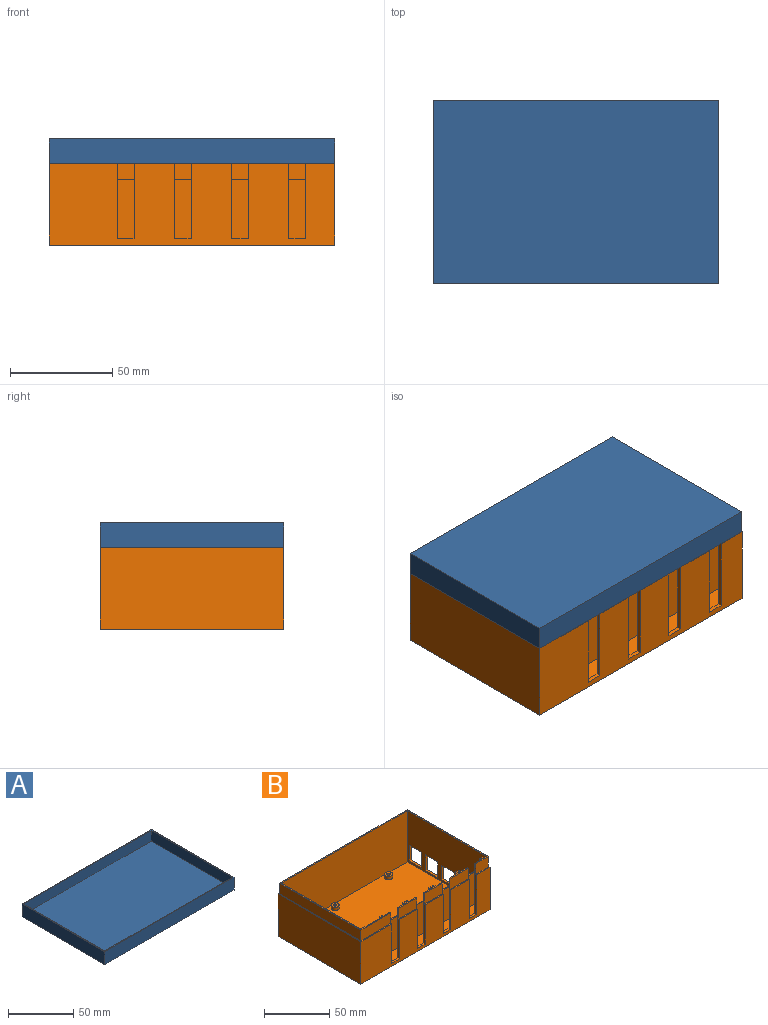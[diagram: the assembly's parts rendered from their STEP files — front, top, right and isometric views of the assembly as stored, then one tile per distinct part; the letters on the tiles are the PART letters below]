
ASSEMBLY  parts=2 mates=1
PART A: 11 faces, bbox 140x90x12 mm
  f0: plane 140x12mm, normal (0,-1,0), area 1680mm2, adj f1,f3,f4,f9
  f1: plane 90x12mm, normal (1,0,0), area 1080mm2, adj f0,f2,f4,f9
  f2: plane 140x12mm, normal (0,1,0), area 1680mm2, adj f1,f3,f4,f9
  f3: plane 90x12mm, normal (-1,0,0), area 1080mm2, adj f0,f2,f4,f9
  f4: plane 140x90mm, normal (0,0,-1), area 12600mm2, adj f0,f1,f2,f3
  f5: plane 88x10mm, normal (1,0,0), area 880mm2, adj f6,f8,f9,f10
  f6: plane 138x10mm, normal (0,-1,0), area 1380mm2, adj f5,f7,f9,f10
  f7: plane 88x10mm, normal (-1,0,0), area 880mm2, adj f6,f8,f9,f10
  f8: plane 138x10mm, normal (0,1,0), area 1380mm2, adj f5,f7,f9,f10
  f9: plane 140x90mm, normal (0,0,1), area 456mm2, adj f0,f1,f2,f3,f5,f6,f7,f8
  f10: plane 138x88mm, normal (0,0,1), area 12144mm2, adj f5,f6,f7,f8
PART B: 118 faces, bbox 140x90x50 mm
  f0: plane 136x75mm, normal (0,0,1), area 10079.2mm2, adj f1,f21,f22,f24,f29,f33,f36,f116
  f1: plane 86x48mm, normal (-1,0,0), area 3495.6mm2, adj f0,f2,f19,f22,f23,f40,f41,f42
  f2: plane 136x48mm, normal (0,1,0), area 4682.4mm2, adj f1,f4,f6,f10,f13,f14,f19,f21
  f3: plane 140x40mm, normal (0,-1,0), area 4386.4mm2, adj f4,f7,f9,f10,f20,f52,f53,f54
  f4: plane 47x2mm, normal (-1,0,0), area 84mm2, adj f2,f3,f14,f59,f107,f108
  f5: plane 38x1mm, normal (-1,0,0), area 38mm2, adj f6,f78,f79,f103
  f6: plane 19.8x3mm, normal (0,0,1), area 25.8mm2, adj f2,f5,f17,f52,f58,f75,f76,f77
  f7: plane 90x40mm, normal (1,0,0), area 2997.6mm2, adj f3,f8,f20,f40,f41,f42,f43,f44
  f8: plane 140x40mm, normal (0,1,0), area 5600mm2, adj f7,f9,f20,f102
  f9: plane 90x40mm, normal (-1,0,0), area 3600mm2, adj f3,f8,f20,f102
  f10: plane 47x2mm, normal (-1,0,0), area 84mm2, adj f2,f3,f19,f61,f101,f102
  f11: plane 38x1mm, normal (-1,0,0), area 38mm2, adj f13,f69,f95,f114
  f12: plane 38x1mm, normal (1,0,0), area 38mm2, adj f14,f71,f91,f112
  f13: plane 19.8x3mm, normal (0,0,1), area 25.8mm2, adj f2,f11,f55,f60,f65,f66,f67,f68
  f14: plane 19.8x3mm, normal (0,0,1), area 25.8mm2, adj f2,f4,f12,f15,f57,f70,f71,f72
  f15: plane 38x1mm, normal (-1,0,0), area 38mm2, adj f14,f73,f93,f111
  f16: plane 38x1mm, normal (-1,0,0), area 38mm2, adj f19,f63,f64,f83
  f17: plane 38x1mm, normal (1,0,0), area 38mm2, adj f6,f74,f76,f87
  f18: plane 38x1mm, normal (1,0,0), area 38mm2, adj f19,f80,f82,f85
  f19: plane 138x88mm, normal (0,0,1), area 361.8mm2, adj f1,f2,f10,f16,f18,f21,f22,f54
  f20: plane 140x90mm, normal (0,0,-1), area 12600mm2, adj f3,f7,f8,f9
  f21: plane 86x48mm, normal (1,0,0), area 4098mm2, adj f0,f2,f19,f22,f23,f115,f116,f117
  f22: plane 136x48mm, normal (0,-1,0), area 6528mm2, adj f0,f1,f19,f21
  f23: plane 136x10mm, normal (0,0,1), area 1360mm2, adj f1,f2,f21,f115
  f24: cylinder r=3.1mm len=6.2mm, axis (0,0,-1), area 58.4mm2, adj f0,f26
  f25: cylinder r=1.38mm len=3mm, axis (0,0,-1), area 25.9mm2, adj f26,f27
  f26: plane 6.2x6.2mm, normal (0,0,1), area 24.3mm2, adj f24,f25
  f27: plane 2.75x2.75mm, normal (0,0,1), area 5.9mm2, adj f25
  f28: cylinder r=1.38mm len=3mm, axis (0,0,-1), area 25.9mm2, adj f30,f31
  f29: cylinder r=3.1mm len=6.2mm, axis (0,0,-1), area 58.4mm2, adj f0,f30
  f30: plane 6.2x6.2mm, normal (0,0,1), area 24.3mm2, adj f28,f29
  f31: plane 2.75x2.75mm, normal (0,0,1), area 5.9mm2, adj f28
  f32: cylinder r=1.38mm len=3mm, axis (0,0,-1), area 25.9mm2, adj f34,f35
  f33: cylinder r=3.1mm len=6.2mm, axis (0,0,-1), area 58.4mm2, adj f0,f34
  f34: plane 6.2x6.2mm, normal (0,0,1), area 24.3mm2, adj f32,f33
  f35: plane 2.75x2.75mm, normal (0,0,1), area 5.9mm2, adj f32
  f36: cylinder r=3.1mm len=6.2mm, axis (0,0,-1), area 58.4mm2, adj f0,f38
  f37: cylinder r=1.38mm len=3mm, axis (0,0,-1), area 25.9mm2, adj f38,f39
  f38: plane 6.2x6.2mm, normal (0,0,1), area 24.3mm2, adj f36,f37
  f39: plane 2.75x2.75mm, normal (0,0,1), area 5.9mm2, adj f37
  f40: plane 13.1x2mm, normal (0,0,-1), area 26.2mm2, adj f1,f7,f41,f43
  f41: plane 14.8x2mm, normal (0,-1,0), area 29.6mm2, adj f1,f7,f40,f42
  f42: plane 13.1x2mm, normal (0,0,1), area 26.2mm2, adj f1,f7,f41,f43
  f43: plane 14.8x2mm, normal (0,1,0), area 29.6mm2, adj f1,f7,f40,f42
  f44: plane 15.9x2mm, normal (0,0,1), area 31.8mm2, adj f1,f7,f45,f47
  f45: plane 13.5x2mm, normal (0,1,0), area 27mm2, adj f1,f7,f44,f46
  f46: plane 15.9x2mm, normal (0,0,-1), area 31.8mm2, adj f1,f7,f45,f47
  f47: plane 13.5x2mm, normal (0,-1,0), area 27mm2, adj f1,f7,f44,f46
  f48: plane 14.8x2mm, normal (0,-1,0), area 29.6mm2, adj f1,f7,f49,f51
  f49: plane 13.1x2mm, normal (0,0,1), area 26.2mm2, adj f1,f7,f48,f50
  f50: plane 14.8x2mm, normal (0,1,0), area 29.6mm2, adj f1,f7,f49,f51
  f51: plane 13.1x2mm, normal (0,0,-1), area 26.2mm2, adj f1,f7,f48,f50
  f52: plane 47x2mm, normal (-1,0,0), area 84mm2, adj f2,f3,f6,f53,f109,f110
  f53: plane 8.2x2mm, normal (0,0,1), area 16.4mm2, adj f2,f3,f52,f54
  f54: plane 47x2mm, normal (1,0,0), area 84mm2, adj f2,f3,f19,f53,f97,f102
  f55: plane 47x2mm, normal (-1,0,0), area 84mm2, adj f2,f3,f13,f56,f105,f106
  f56: plane 8.2x2mm, normal (0,0,1), area 16.4mm2, adj f2,f3,f55,f57
  f57: plane 47x2mm, normal (1,0,0), area 84mm2, adj f2,f3,f14,f56,f107,f108
  f58: plane 47x2mm, normal (1,0,0), area 84mm2, adj f2,f3,f6,f59,f109,f110
  f59: plane 8.2x2mm, normal (0,0,1), area 16.4mm2, adj f2,f3,f4,f58
  f60: plane 47x2mm, normal (1,0,0), area 84mm2, adj f2,f3,f13,f61,f105,f106
  f61: plane 8.2x2mm, normal (0,0,1), area 16.4mm2, adj f2,f3,f10,f60
  f62: plane 38x2mm, normal (1,0,0), area 76mm2, adj f2,f19,f63,f64
  f63: plane 2x2mm, normal (0,0,-1), area 3mm2, adj f2,f16,f62,f64,f83,f84
  f64: plane 38x2mm, normal (0,1,0), area 76mm2, adj f16,f19,f62,f63
  f65: plane 38x1mm, normal (1,0,0), area 38mm2, adj f13,f67,f89,f113
  f66: plane 38x2mm, normal (-1,0,0), area 76mm2, adj f2,f13,f67,f113
  f67: plane 38x2mm, normal (0,1,0), area 76mm2, adj f13,f65,f66,f113
  f68: plane 38x2mm, normal (1,0,0), area 76mm2, adj f2,f13,f69,f114
  f69: plane 38x2mm, normal (0,1,0), area 76mm2, adj f11,f13,f68,f114
  f70: plane 38x2mm, normal (-1,0,0), area 76mm2, adj f2,f14,f71,f112
  f71: plane 38x2mm, normal (0,1,0), area 76mm2, adj f12,f14,f70,f112
  f72: plane 38x2mm, normal (1,0,0), area 76mm2, adj f2,f14,f73,f111
  f73: plane 38x2mm, normal (0,1,0), area 76mm2, adj f14,f15,f72,f111
  f74: plane 2x2mm, normal (0,0,-1), area 3mm2, adj f2,f17,f75,f76,f87,f88
  f75: plane 38x2mm, normal (-1,0,0), area 76mm2, adj f2,f6,f74,f76
  f76: plane 38x2mm, normal (0,1,0), area 76mm2, adj f6,f17,f74,f75
  f77: plane 38x2mm, normal (1,0,0), area 76mm2, adj f2,f6,f78,f79
  f78: plane 2x2mm, normal (0,0,-1), area 3mm2, adj f2,f5,f77,f79,f103,f104
  f79: plane 38x2mm, normal (0,1,0), area 76mm2, adj f5,f6,f77,f78
  f80: plane 2x2mm, normal (0,0,-1), area 3mm2, adj f2,f18,f81,f82,f85,f86
  f81: plane 38x2mm, normal (-1,0,0), area 76mm2, adj f2,f19,f80,f82
  f82: plane 38x2mm, normal (0,1,0), area 76mm2, adj f18,f19,f80,f81
  f83: plane 38x1mm, normal (0,-1,0), area 38mm2, adj f16,f19,f63,f84
  f84: plane 38x1mm, normal (-1,0,0), area 38mm2, adj f2,f19,f63,f83
  f85: plane 38x1mm, normal (0,-1,0), area 38mm2, adj f18,f19,f80,f86
  f86: plane 38x1mm, normal (1,0,0), area 38mm2, adj f2,f19,f80,f85
  f87: plane 38x1mm, normal (0,-1,0), area 38mm2, adj f6,f17,f74,f88
  f88: plane 38x1mm, normal (1,0,0), area 38mm2, adj f2,f6,f74,f87
  f89: plane 38x1mm, normal (0,-1,0), area 38mm2, adj f13,f65,f90,f113
  f90: plane 38x1mm, normal (1,0,0), area 38mm2, adj f2,f13,f89,f113
  f91: plane 38x1mm, normal (0,-1,0), area 38mm2, adj f12,f14,f92,f112
  f92: plane 38x1mm, normal (1,0,0), area 38mm2, adj f2,f14,f91,f112
  f93: plane 38x1mm, normal (0,-1,0), area 38mm2, adj f14,f15,f94,f111
  f94: plane 38x1mm, normal (-1,0,0), area 38mm2, adj f2,f14,f93,f111
  f95: plane 38x1mm, normal (0,-1,0), area 38mm2, adj f11,f13,f96,f114
  f96: plane 38x1mm, normal (-1,0,0), area 38mm2, adj f2,f13,f95,f114
  f97: plane 32.4x10mm, normal (0,-1,0), area 324mm2, adj f19,f54,f98,f102
  f98: plane 88x10mm, normal (-1,0,0), area 880mm2, adj f19,f97,f99,f102
  f99: plane 138x10mm, normal (0,1,0), area 1380mm2, adj f19,f98,f100,f102
  f100: plane 88x10mm, normal (1,0,0), area 880mm2, adj f19,f99,f101,f102
  f101: plane 13.4x10mm, normal (0,-1,0), area 134mm2, adj f10,f19,f100,f102
  f102: plane 140x90mm, normal (0,0,1), area 363.8mm2, adj f3,f7,f8,f9,f10,f54,f97,f98
  f103: plane 38x1mm, normal (0,-1,0), area 38mm2, adj f5,f6,f78,f104
  f104: plane 38x1mm, normal (-1,0,0), area 38mm2, adj f2,f6,f78,f103
  f105: plane 19.8x10mm, normal (0,-1,0), area 198mm2, adj f13,f55,f60,f106
  f106: plane 19.8x1mm, normal (0,0,1), area 19.8mm2, adj f3,f55,f60,f105
  f107: plane 19.8x10mm, normal (0,-1,0), area 198mm2, adj f4,f14,f57,f108
  f108: plane 19.8x1mm, normal (0,0,1), area 19.8mm2, adj f3,f4,f57,f107
  f109: plane 19.8x10mm, normal (0,-1,0), area 198mm2, adj f6,f52,f58,f110
  f110: plane 19.8x1mm, normal (0,0,1), area 19.8mm2, adj f3,f52,f58,f109
  f111: plane 2x2mm, normal (0,0,-1), area 3mm2, adj f2,f15,f72,f73,f93,f94
  f112: plane 2x2mm, normal (0,0,-1), area 3mm2, adj f2,f12,f70,f71,f91,f92
  f113: plane 2x2mm, normal (0,0,-1), area 3mm2, adj f2,f65,f66,f67,f89,f90
  f114: plane 2x2mm, normal (0,0,-1), area 3mm2, adj f2,f11,f68,f69,f95,f96
  f115: plane 136x30mm, normal (0,-1,0), area 4080mm2, adj f1,f21,f23,f117
  f116: plane 136x30mm, normal (0,1,0), area 4080mm2, adj f0,f1,f21,f117
  f117: plane 136x1mm, normal (0,0,1), area 136mm2, adj f1,f21,f115,f116
PLACE A rot(axis=(1,0,0),180deg) t=(48.63,-19.48,22.53)mm
PLACE B t=(48.63,-20.6,-29.47)mm
MATE fastened B.f102 <-> A.f9  axis (0,0,1) through (-21.37,-64.48,10.53)mm
